FCSTD DOCUMENT  (FreeCAD 0.19R24276 (Git))
Label: pinci
License: All rights reserved
LicenseURL: http://en.wikipedia.org/wiki/All_rights_reserved
objects: Sketcher::SketchObject×1, PartDesign::Body×1
note: 2 computed .brp shape members not serialized (recipe doc carries the construction recipe); baked Part::Feature solids carry a one-line shape summary decoded from their .brp

FEATURE [Sketcher::SketchObject] Sketch
  FullyConstrained = true
  MapMode = 5
  Support = -> [XY_Plane]
  sketch-geometry (109):
    g0: LineSegment StartX=0 StartY=0 StartZ=0 EndX=114 EndY=0 EndZ=0
    g1: LineSegment StartX=114 StartY=0 StartZ=0 EndX=114 EndY=-88.5414 EndZ=0
    g2: LineSegment StartX=114 StartY=-88.5414 StartZ=0 EndX=0 EndY=-88.5414 EndZ=0
    g3: LineSegment StartX=0 StartY=-88.5414 StartZ=0 EndX=0 EndY=0 EndZ=0
    g4: LineSegment StartX=25 StartY=-7 StartZ=0 EndX=43 EndY=-7 EndZ=0
    g5: LineSegment StartX=43 StartY=-7 StartZ=0 EndX=43 EndY=-24 EndZ=0
    g6: LineSegment StartX=43 StartY=-24 StartZ=0 EndX=25 EndY=-24 EndZ=0
    g7: LineSegment StartX=25 StartY=-24 StartZ=0 EndX=25 EndY=-7 EndZ=0
    g8: LineSegment StartX=43 StartY=-4.5 StartZ=0 EndX=61 EndY=-4.5 EndZ=0
    g9: LineSegment StartX=61 StartY=-4.5 StartZ=0 EndX=61 EndY=-21.5 EndZ=0
    g10: LineSegment StartX=61 StartY=-21.5 StartZ=0 EndX=43 EndY=-21.5 EndZ=0
    g11: LineSegment StartX=43 StartY=-21.5 StartZ=0 EndX=43 EndY=-4.5 EndZ=0
    g12: LineSegment StartX=61 StartY=1 StartZ=0 EndX=79 EndY=1 EndZ=0
    g13: LineSegment StartX=79 StartY=1 StartZ=0 EndX=79 EndY=-16 EndZ=0
    g14: LineSegment StartX=79 StartY=-16 StartZ=0 EndX=61 EndY=-16 EndZ=0
    g15: LineSegment StartX=61 StartY=-16 StartZ=0 EndX=61 EndY=1 EndZ=0
    g16: LineSegment StartX=79 StartY=-6 StartZ=0 EndX=97 EndY=-6 EndZ=0
    g17: LineSegment StartX=97 StartY=-6 StartZ=0 EndX=97 EndY=-23 EndZ=0
    g18: LineSegment StartX=97 StartY=-23 StartZ=0 EndX=79 EndY=-23 EndZ=0
    g19: LineSegment StartX=79 StartY=-23 StartZ=0 EndX=79 EndY=-6 EndZ=0
    g20: LineSegment StartX=97 StartY=-18 StartZ=0 EndX=115 EndY=-18 EndZ=0
    g21: LineSegment StartX=115 StartY=-18 StartZ=0 EndX=115 EndY=-35 EndZ=0
    g22: LineSegment StartX=115 StartY=-35 StartZ=0 EndX=97 EndY=-35 EndZ=0
    g23: LineSegment StartX=97 StartY=-35 StartZ=0 EndX=97 EndY=-18 EndZ=0
    g24: LineSegment StartX=0 StartY=0 StartZ=0 EndX=25 EndY=0 EndZ=0
    g25: LineSegment StartX=25 StartY=0 StartZ=0 EndX=25 EndY=-55 EndZ=0
    g26: LineSegment StartX=25 StartY=-55 StartZ=0 EndX=0 EndY=-55 EndZ=0
    g27: LineSegment StartX=0 StartY=-55 StartZ=0 EndX=0 EndY=0 EndZ=0
    g28: LineSegment StartX=25 StartY=-24 StartZ=0 EndX=25 EndY=-41 EndZ=0
    g29: LineSegment StartX=25 StartY=-41 StartZ=0 EndX=25 EndY=-58 EndZ=0
    g30: LineSegment StartX=25 StartY=-58 StartZ=0 EndX=43 EndY=-58 EndZ=0
    g31: LineSegment StartX=43 StartY=-58 StartZ=0 EndX=43 EndY=-41 EndZ=0
    g32: LineSegment StartX=43 StartY=-41 StartZ=0 EndX=43 EndY=-24 EndZ=0
    g33: LineSegment StartX=25 StartY=-41 StartZ=0 EndX=43 EndY=-41 EndZ=0
    g34: LineSegment StartX=43 StartY=-21.5 StartZ=0 EndX=43 EndY=-38.5 EndZ=0
    g35: LineSegment StartX=43 StartY=-38.5 StartZ=0 EndX=43 EndY=-55.5 EndZ=0
    g36: LineSegment StartX=43 StartY=-55.5 StartZ=0 EndX=61 EndY=-55.5 EndZ=0
    g37: LineSegment StartX=61 StartY=-55.5 StartZ=0 EndX=61 EndY=-38.5 EndZ=0
    g38: LineSegment StartX=61 StartY=-38.5 StartZ=0 EndX=61 EndY=-21.5 EndZ=0
    g39: LineSegment StartX=61 StartY=-16 StartZ=0 EndX=61 EndY=-33 EndZ=0
    g40: LineSegment StartX=61 StartY=-33 StartZ=0 EndX=61 EndY=-50 EndZ=0
    g41: LineSegment StartX=61 StartY=-50 StartZ=0 EndX=79 EndY=-50 EndZ=0
    g42: LineSegment StartX=79 StartY=-50 StartZ=0 EndX=79 EndY=-33 EndZ=0
    g43: LineSegment StartX=79 StartY=-33 StartZ=0 EndX=79 EndY=-16 EndZ=0
    g44: LineSegment StartX=79 StartY=-23 StartZ=0 EndX=79 EndY=-40 EndZ=0
    g45: LineSegment StartX=79 StartY=-40 StartZ=0 EndX=79 EndY=-57 EndZ=0
    g46: LineSegment StartX=79 StartY=-57 StartZ=0 EndX=97 EndY=-57 EndZ=0
    g47: LineSegment StartX=97 StartY=-57 StartZ=0 EndX=97 EndY=-40 EndZ=0
    g48: LineSegment StartX=97 StartY=-40 StartZ=0 EndX=97 EndY=-23 EndZ=0
    g49: LineSegment StartX=97 StartY=-35 StartZ=0 EndX=97 EndY=-52 EndZ=0
    g50: LineSegment StartX=97 StartY=-52 StartZ=0 EndX=97 EndY=-69 EndZ=0
    g51: LineSegment StartX=97 StartY=-69 StartZ=0 EndX=115 EndY=-69 EndZ=0
    g52: LineSegment StartX=115 StartY=-69 StartZ=0 EndX=115 EndY=-52 EndZ=0
    g53: LineSegment StartX=115 StartY=-52 StartZ=0 EndX=115 EndY=-35 EndZ=0
    g54: LineSegment StartX=43 StartY=-38.5 StartZ=0 EndX=61 EndY=-38.5 EndZ=0
    g55: LineSegment StartX=61 StartY=-33 StartZ=0 EndX=79 EndY=-33 EndZ=0
    g56: LineSegment StartX=79 StartY=-40 StartZ=0 EndX=97 EndY=-40 EndZ=0
    g57: LineSegment StartX=97 StartY=-52 StartZ=0 EndX=115 EndY=-52 EndZ=0
    g58: LineSegment StartX=5.24648 StartY=-78.065 StartZ=0 EndX=15.5954 EndY=-91.552 EndZ=0
    g59: LineSegment StartX=15.5954 StartY=-91.552 StartZ=0 EndX=29.8758 EndY=-80.5943 EndZ=0
    g60: LineSegment StartX=29.8758 StartY=-80.5943 StartZ=0 EndX=19.5268 EndY=-67.1072 EndZ=0
    g61: LineSegment StartX=19.5268 StartY=-67.1072 StartZ=0 EndX=5.24648 EndY=-78.065 EndZ=0
    g62: LineSegment StartX=23.3702 StartY=-64.8883 StartZ=0 EndX=29.8758 EndY=-80.5943 EndZ=0
    g63: LineSegment StartX=29.8758 StartY=-80.5943 StartZ=0 EndX=46.5056 EndY=-73.706 EndZ=0
    g64: LineSegment StartX=46.5056 StartY=-73.706 StartZ=0 EndX=40 EndY=-58 EndZ=0
    g65: LineSegment StartX=40 StartY=-58 StartZ=0 EndX=23.3702 EndY=-64.8883 EndZ=0
    g66: ArcOfCircle CenterX=2 CenterY=-2 CenterZ=0 NormalX=0 NormalY=0 NormalZ=1 AngleXU=0 Radius=2 StartAngle=1.5708 EndAngle=3.14159
    g67: ArcOfCircle CenterX=10 CenterY=-66.1904 CenterZ=0 NormalX=0 NormalY=0 NormalZ=1 AngleXU=0 Radius=10 StartAngle=3.14159 EndAngle=3.79609
    g68: ArcOfCircle CenterX=16.5184 CenterY=-84.5414 CenterZ=0 NormalX=0 NormalY=0 NormalZ=1 AngleXU=0 Radius=4 StartAngle=3.79609 EndAngle=5.36688
    g69: Circle CenterX=18.9534 CenterY=-87.7148 CenterZ=0 NormalX=0 NormalY=0 NormalZ=1 AngleXU=0 Radius=1
    g70: Circle CenterX=44.6463 CenterY=-68 CenterZ=0 NormalX=0 NormalY=0 NormalZ=1 AngleXU=0 Radius=1
    g71: Circle CenterX=112 CenterY=-68 CenterZ=0 NormalX=0 NormalY=0 NormalZ=1 AngleXU=0 Radius=1
    g72: BSplineCurve PolesCount=3 KnotsCount=2 Degree=2 IsPeriodic=0
    g73: GeomPoint X=18.9534 Y=-87.7148 Z=0
    g74: GeomPoint X=112 Y=-68 Z=0
    g75: LineSegment StartX=2.06647 StartY=-72.278 StartZ=0 EndX=13.345 EndY=-86.9764 EndZ=0
    g76: LineSegment StartX=0 StartY=-2 StartZ=0 EndX=0 EndY=-66.1904 EndZ=0
    g77: LineSegment StartX=18.9534 StartY=-87.7148 StartZ=0 EndX=44.6463 EndY=-68 EndZ=0
    g78: LineSegment StartX=44.6463 StartY=-68 StartZ=0 EndX=112 EndY=-68 EndZ=0
    g79: ArcOfCircle CenterX=112 CenterY=-66 CenterZ=0 NormalX=0 NormalY=0 NormalZ=1 AngleXU=0 Radius=2 StartAngle=4.71239 EndAngle=6.28319
    g80: LineSegment StartX=2 StartY=0 StartZ=0 EndX=49 EndY=0 EndZ=0
    g81: ArcOfCircle CenterX=49 CenterY=-5 CenterZ=0 NormalX=0 NormalY=0 NormalZ=1 AngleXU=0 Radius=5 StartAngle=1.5708 EndAngle=1.5708
    g82: ArcOfCircle CenterX=104 CenterY=-22.4202 CenterZ=0 NormalX=0 NormalY=0 NormalZ=1 AngleXU=0 Radius=10 StartAngle=1.41484e-07 EndAngle=0.349066
    g83: LineSegment StartX=114 StartY=-22.4202 StartZ=0 EndX=114 EndY=-66 EndZ=0
    g84: Circle CenterX=49 CenterY=-3.91e-14 CenterZ=0 NormalX=0 NormalY=0 NormalZ=1 AngleXU=0 Radius=1
    g85: Circle CenterX=106.481 CenterY=-1.33e-14 CenterZ=0 NormalX=0 NormalY=0 NormalZ=1 AngleXU=0 Radius=1
    g86: Circle CenterX=113.397 CenterY=-19 CenterZ=0 NormalX=0 NormalY=0 NormalZ=1 AngleXU=0 Radius=1
    g87: BSplineCurve PolesCount=3 KnotsCount=2 Degree=2 IsPeriodic=0
    g88: GeomPoint X=49 Y=-3.91e-14 Z=0
    g89: GeomPoint X=113.397 Y=-19 Z=0
    g90: LineSegment StartX=49 StartY=-3.91e-14 StartZ=0 EndX=106.481 EndY=-1.33e-14 EndZ=0
    g91: LineSegment StartX=106.481 StartY=-1.33e-14 StartZ=0 EndX=113.397 EndY=-19 EndZ=0
    g92: GeomPoint X=17.5611 Y=-79.3296 Z=0
    g93: GeomPoint X=34.9379 Y=-69.2971 Z=0
    g94: GeomPoint X=34 Y=-15.5 Z=0
    g95: GeomPoint X=34 Y=-32.5 Z=0
    g96: GeomPoint X=34 Y=-49.5 Z=0
    g97: GeomPoint X=52 Y=-47 Z=0
    g98: GeomPoint X=52 Y=-30 Z=0
    g99: GeomPoint X=52 Y=-13 Z=0
    g100: GeomPoint X=70 Y=-7.5 Z=0
    g101: GeomPoint X=70 Y=-24.5 Z=0
    g102: GeomPoint X=70 Y=-41.5 Z=0
    g103: GeomPoint X=88 Y=-48.5 Z=0
    g104: GeomPoint X=88 Y=-31.5 Z=0
    g105: GeomPoint X=88 Y=-14.5 Z=0
    g106: GeomPoint X=106 Y=-26.5 Z=0
    g107: GeomPoint X=106 Y=-43.5 Z=0
    g108: GeomPoint X=106 Y=-60.5 Z=0
  constraints (278):
    c: Coincident(g0,g1)
    c: Coincident(g1,g2)
    c: Coincident(g2,g3)
    c: Coincident(g3,g0)
    c: Horizontal(g0)
    c: Horizontal(g2)
    c: Vertical(g1)
    c: Vertical(g3)
    c: Coincident(g0,g-1)
    c: Coincident(g4,g5)
    c: Coincident(g5,g6)
    c: Coincident(g6,g7)
    c: Coincident(g7,g4)
    c: Horizontal(g4)
    c: Horizontal(g6)
    c: Vertical(g5)
    c: Vertical(g7)
    c: Coincident(g8,g9)
    c: Coincident(g9,g10)
    c: Coincident(g10,g11)
    c: Coincident(g11,g8)
    c: Horizontal(g8)
    c: Horizontal(g10)
    c: Vertical(g9)
    c: Vertical(g11)
    c: Coincident(g12,g13)
    c: Coincident(g13,g14)
    c: Coincident(g14,g15)
    c: Coincident(g15,g12)
    c: Horizontal(g12)
    c: Horizontal(g14)
    c: Vertical(g13)
    c: Vertical(g15)
    c: Coincident(g16,g17)
    c: Coincident(g17,g18)
    c: Coincident(g18,g19)
    c: Coincident(g19,g16)
    c: Horizontal(g16)
    c: Horizontal(g18)
    c: Vertical(g17)
    c: Vertical(g19)
    c: Coincident(g20,g21)
    c: Coincident(g21,g22)
    c: Coincident(g22,g23)
    c: Coincident(g23,g20)
    c: Horizontal(g20)
    c: Horizontal(g22)
    c: Vertical(g21)
    c: Vertical(g23)
    c: Equal(g4,g8)
    c: Equal(g8,g12)
    c: Equal(g12,g16)
    c: Equal(g16,g20)
    c: Equal(g5,g9)
    c: Equal(g9,g13)
    c: Equal(g13,g17)
    c: Equal(g17,g21)
    c: PointOnObject(g4,g11)
    c: PointOnObject(g8,g15)
    c: PointOnObject(g12,g19)
    c: PointOnObject(g16,g23)
    c: DistanceX(g4,g4) = 18
    c: DistanceY(g7,g7) = 17
    c: DistanceY(g20,g16) = 12
    c: DistanceY(g16,g12) = 7
    c: DistanceY(g8,g12) = 5.5
    c: DistanceY(g4,g8) = 2.5
    c: Coincident(g24,g25)
    c: Coincident(g25,g26)
    c: Coincident(g26,g27)
    c: Coincident(g27,g24)
    c: Horizontal(g24)
    c: Horizontal(g26)
    c: Vertical(g25)
    c: Vertical(g27)
    c: DistanceX(g24,g24) = 25
    c: DistanceY(g25,g25) = 55
    c: Coincident(g24,g-1)
    c: PointOnObject(g4,g25)
    c: Coincident(g28,g29)
    c: Coincident(g29,g30)
    c: Coincident(g30,g31)
    c: Coincident(g31,g32)
    c: Coincident(g33,g28)
    c: Coincident(g33,g31)
    c: Horizontal(g33)
    c: Vertical(g28)
    c: Vertical(g29)
    c: Vertical(g31)
    c: Vertical(g32)
    c: Horizontal(g30)
    c: Equal(g5,g32)
    c: Equal(g32,g31)
    c: Coincident(g28,g6)
    c: Coincident(g32,g5)
    c: Coincident(g34,g35)
    c: Coincident(g35,g36)
    c: Coincident(g36,g37)
    c: Coincident(g37,g38)
    c: Coincident(g39,g40)
    c: Coincident(g40,g41)
    c: Coincident(g41,g42)
    c: Coincident(g42,g43)
    c: Coincident(g44,g45)
    c: Coincident(g45,g46)
    c: Coincident(g46,g47)
    c: Coincident(g47,g48)
    c: Coincident(g49,g50)
    c: Coincident(g50,g51)
    c: Coincident(g51,g52)
    c: Coincident(g52,g53)
    c: Horizontal(g54)
    c: Horizontal(g36)
    c: Horizontal(g41)
    c: Horizontal(g55)
    c: Horizontal(g56)
    c: Horizontal(g46)
    c: Horizontal(g51)
    c: Horizontal(g57)
    c: Vertical(g34)
    c: Vertical(g35)
    c: Vertical(g37)
    c: Vertical(g38)
    c: Vertical(g39)
    c: Vertical(g40)
    c: Vertical(g42)
    c: Vertical(g43)
    c: Vertical(g44)
    c: Vertical(g45)
    c: Vertical(g48)
    c: Vertical(g47)
    c: Vertical(g49)
    c: Vertical(g50)
    c: Vertical(g52)
    c: Vertical(g53)
    c: Equal(g5,g38)
    c: Equal(g5,g43)
    c: Equal(g5,g48)
    c: Equal(g5,g53)
    c: Equal(g5,g37)
    c: Equal(g5,g42)
    c: Equal(g5,g47)
    c: Equal(g5,g52)
    c: Equal(g6,g36)
    c: Equal(g6,g41)
    c: Equal(g6,g46)
    c: Equal(g6,g51)
    c: Coincident(g54,g34)
    c: Coincident(g54,g37)
    c: Coincident(g38,g9)
    c: PointOnObject(g34,g10)
    c: Coincident(g55,g39)
    c: Coincident(g39,g14)
    c: Coincident(g42,g55)
    c: PointOnObject(g43,g14)
    c: Coincident(g56,g47)
    c: Coincident(g56,g44)
    c: Coincident(g44,g18)
    c: PointOnObject(g48,g18)
    c: Coincident(g57,g52)
    c: Coincident(g57,g49)
    c: Coincident(g49,g22)
    c: PointOnObject(g53,g22)
    c: Coincident(g58,g59)
    c: Coincident(g59,g60)
    c: Coincident(g60,g61)
    c: Coincident(g61,g58)
    c: Coincident(g62,g63)
    c: Coincident(g63,g64)
    c: Coincident(g64,g65)
    c: Coincident(g65,g62)
    c: Perpendicular(g61,g60)
    c: Perpendicular(g58,g61)
    c: Perpendicular(g59,g58)
    c: Perpendicular(g63,g62)
    c: Perpendicular(g64,g63)
    c: Perpendicular(g65,g64)
    c: Equal(g4,g61)
    c: Equal(g4,g65)
    c: Equal(g5,g60)
    c: Equal(g5,g64)
    c: Angle(g2,g59) = 0.654498
    c: Angle(g2,g63) = 0.392699
    c: Coincident(g59,g62)
    c: PointOnObject(g64,g30)
    c: DistanceX(g64,g30) = 3
    c: DistanceY(g0,g12) = 1
    c: DistanceX(g0,g20) = 1
    c: Weight(g69) = 1
    c: Equal(g69,g70)
    c: Equal(g69,g71)
    c: InternalAlignment(g69,g72)
    c: InternalAlignment(g70,g72)
    c: InternalAlignment(g71,g72)
    c: InternalAlignment(g73,g72)
    c: InternalAlignment(g74,g72)
    c: Parallel(g75,g58)
    c: Distance(g58,g75) = 1
    c: PointOnObject(g76,g3)
    c: PointOnObject(g76,g3)
    c: Radius(g66) = 2
    c: Coincident(g66,g76)
    c: Tangent(g66,g76)
    c: Tangent(g66,g0)
    c: PointOnObject(g66,g0)
    c: Coincident(g67,g76)
    c: Tangent(g67,g3)
    c: Tangent(g67,g75)
    c: Coincident(g75,g67)
    c: Coincident(g68,g75)
    c: Tangent(g68,g75)
    c: Coincident(g72,g68)
    c: Distance(g68,g59) = 1
    c: Coincident(g77,g70)
    c: Coincident(g77,g68)
    c: Tangent(g77,g68)
    c: Parallel(g77,g59)
    c: Equal(g79,g66)
    c: Coincident(g80,g66)
    c: Coincident(g81,g80)
    c: Tangent(g81,g80)
    c: PointOnObject(g80,g0)
    c: Coincident(g83,g82)
    c: Distance(g81,g13) = 30
    c: Tangent(g82,g83)
    c: PointOnObject(g82,g1)
    c: Coincident(g78,g70)
    c: Coincident(g78,g72)
    c: Coincident(g83,g79)
    c: Tangent(g79,g83)
    c: PointOnObject(g79,g1)
    c: Horizontal(g78)
    c: Coincident(g72,g79)
    c: Tangent(g79,g78)
    c: Distance(g72,g51) = 1
    c: Tangent(g2,g68)
    c: Weight(g84) = 1
    c: Equal(g84,g85)
    c: Equal(g84,g86)
    c: InternalAlignment(g84,g87)
    c: InternalAlignment(g85,g87)
    c: InternalAlignment(g86,g87)
    c: InternalAlignment(g88,g87)
    c: InternalAlignment(g89,g87)
    c: Coincident(g91,g90)
    c: Coincident(g90,g85)
    c: Coincident(g90,g87)
    c: Coincident(g91,g87)
    c: Angle(g0,g90) = 3.14159
    c: Angle(g91,g1) = 2.79253
    c: Coincident(g87,g81)
    c: Tangent(g90,g81)
    c: DistanceY(g82,g20) = 1
    c: Coincident(g82,g87)
    c: Tangent(g82,g91)
    c: Radius(g81) = 5
    c: Radius(g82) = 10
    c: Radius(g67) = 10
    c: Radius(g68) = 4
    c: DistanceY(g1,g1) = 88.5414
    c: DistanceX(g2,g2) = 114
    c: Symmetric(g58,g59,g92)
    c: Symmetric(g62,g63,g93)
    c: Symmetric(g4,g5,g94)
    c: Symmetric(g6,g31,g95)
    c: Symmetric(g28,g30,g96)
    c: Symmetric(g34,g36,g97)
    c: Symmetric(g10,g37,g98)
    c: Symmetric(g8,g9,g99)
    c: Symmetric(g12,g13,g100)
    c: Symmetric(g14,g42,g101)
    c: Symmetric(g39,g41,g102)
    c: Symmetric(g16,g17,g105)
    c: Symmetric(g18,g47,g104)
    c: Symmetric(g44,g46,g103)
    c: Symmetric(g20,g21,g106)
    c: Symmetric(g22,g52,g107)
    c: Symmetric(g49,g51,g108)
FEATURE [PartDesign::Body] Body  label="pcb_edge_cuts"
  Group = -> [Sketch]
  Origin = -> Origin
